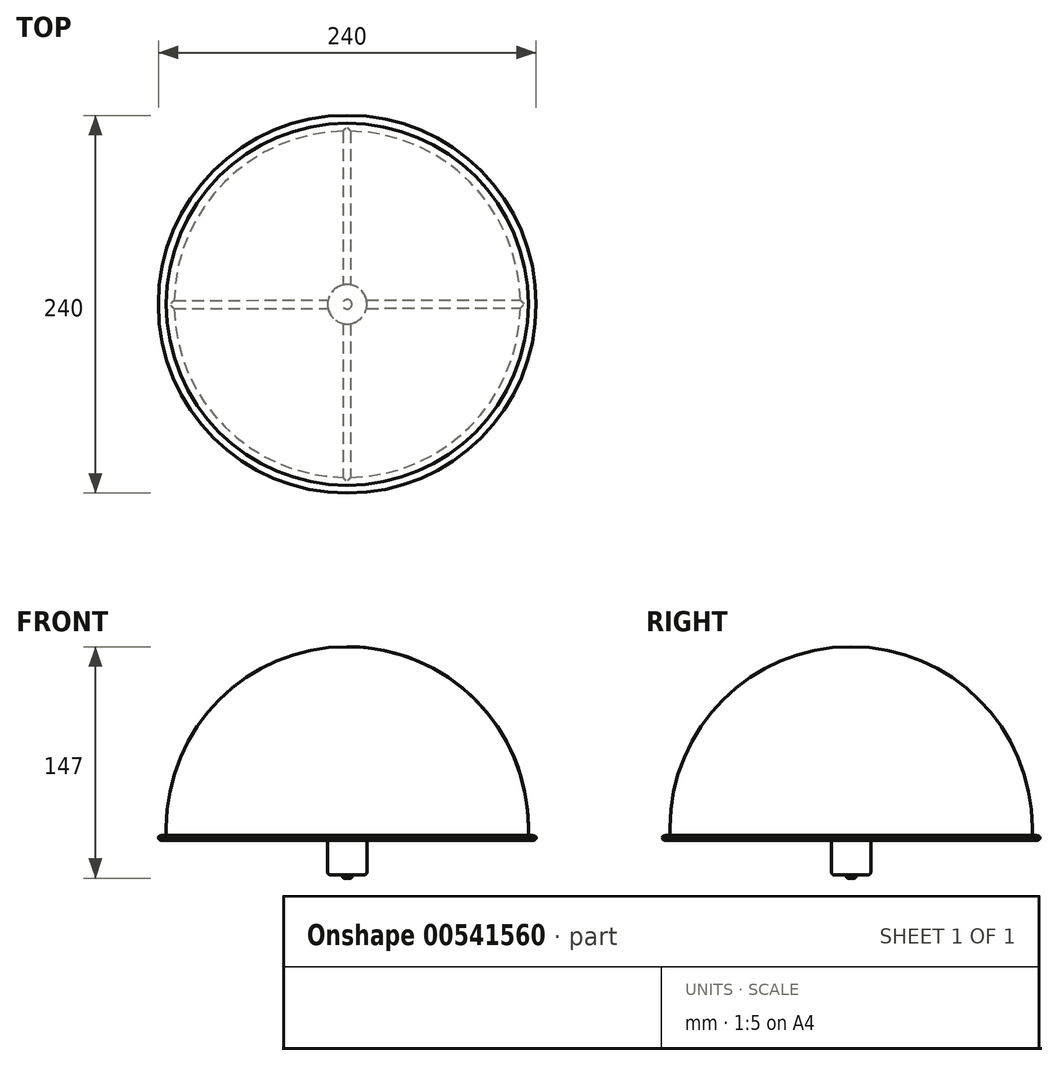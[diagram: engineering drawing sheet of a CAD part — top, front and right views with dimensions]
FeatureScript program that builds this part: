
annotation { "Feature Type Name" : "Feature", "Feature Type Description" : "" }
export const myFeature = defineFeature(function(context is Context, id is Id, definition is map)
    precondition{}
    {
        {
            var Q0;
            Q0=qCreatedBy(makeId("Top.planeOp"),FACE);
            var sketch = newSketch(context, id + "F0", { "sketchPlane" : qUnion([Q0])});
            skCircle(sketch, "E0", {"center": v(0, 0) * mm, "radius": 115 * mm});
            skSolve(sketch);
        }
        {
            var Q0;
            Q0 = qSketchRegion(id + "F0", true);
            extrude(context, id + "F1", {"entities" : qUnion([Q0]), "depth" : 120 * mm, "offsetDistance" : 25 * mm});
        }
        {
            var Q0;
            Q0=makeQuery(id+"F1.opExtrude","CAP_EDGE",EDGE,{"disambiguationData":[OSD([sQuery(id+"F0.wireOp",EDGE,"E0")])],"isStart":false});
            fillet(context, id + "F2", {"entities" : qUnion([Q0]), "radius" : 115 * mm, "tangentPropagation" : true, "allowEdgeOverflow" : false});
        }
        {
            var Q0;
            Q0=makeQuery(id+"F1.opExtrude","CAP_FACE",FACE,{"disambiguationData":[OSD([sQuery(id+"F0.wireOp",EDGE,"E0")])],"isStart":true});
            var sketch = newSketch(context, id + "F3", { "sketchPlane" : qUnion([Q0])});
            skCircle(sketch, "E1", {"center": v(0, 0) * mm, "radius": 120 * mm});
            skArc(sketch, "E2", {"start": v(2.2, -109.98) * mm, "mid": v(77.64, -77.93) * mm, "end": v(109.97, -2.6) * mm});
            skLineSegment(sketch, "E3.left", {"start": v(-2.8, -109.96) * mm, "end": v(-2.8, -2.56) * mm});
            skLineSegment(sketch, "E3.right", {"start": v(2.2, -109.98) * mm, "end": v(2.2, -2.56) * mm});
            skPoint(sketch, "E3.middle", {"position": v(-0.3, 15.02) * mm});
            skLineSegment(sketch, "E4.1.0", {"start": v(-109.97, -2.5) * mm, "end": v(-2.8, -2.56) * mm});
            skLineSegment(sketch, "E4.1.1", {"start": v(-109.96, 2.8) * mm, "end": v(-2.8, 2.6) * mm});
            skLineSegment(sketch, "E4.anchor1", {"start": v(0, 0) * mm, "end": v(2.4, -119.98) * mm, "construction": true});
            skLineSegment(sketch, "E4.anchor2", {"start": v(0, 0) * mm, "end": v(-125, -2.5) * mm, "construction": true});
            skPoint(sketch, "E5.orphan", {"position": v(2.2, -109.98) * mm});
            skPoint(sketch, "E6.orphan", {"position": v(-2.8, -109.97) * mm});
            skPoint(sketch, "E7.orphan", {"position": v(125, 2.36) * mm});
            skPoint(sketch, "E8.orphan", {"position": v(129.97, -2.62) * mm});
            skArc(sketch, "E9.trimOffspring", {"start": v(109.97, 2.4) * mm, "mid": v(77.71, 77.85) * mm, "end": v(2.2, 109.98) * mm});
            skPoint(sketch, "E10.orphan", {"position": v(2.2, 140.01) * mm});
            skPoint(sketch, "E11.orphan", {"position": v(-2.8, 140.02) * mm});
            skArc(sketch, "E12.trimOffspring", {"start": v(-2.8, 109.96) * mm, "mid": v(-77.78, 77.78) * mm, "end": v(-109.96, 2.8) * mm});
            skArc(sketch, "E13.trimOffspring", {"start": v(-109.98, -2.2) * mm, "mid": v(-78, -77.57) * mm, "end": v(-2.8, -109.96) * mm});
            skLineSegment(sketch, "E14.trimOffspring", {"start": v(2.2, 2.6) * mm, "end": v(2.2, 109.98) * mm});
            skLineSegment(sketch, "E15.trimOffspring", {"start": v(2.2, 2.6) * mm, "end": v(109.97, 2.4) * mm});
            skLineSegment(sketch, "E16.trimOffspring", {"start": v(-2.8, 2.6) * mm, "end": v(-2.8, 109.96) * mm});
            skLineSegment(sketch, "E17.trimOffspring", {"start": v(2.2, -2.56) * mm, "end": v(109.97, -2.6) * mm});
            skSolve(sketch);
        }
        {
            var Q0;
            Q0 = qSketchRegion(id + "F3", true);
            extrude(context, id + "F4", {"entities" : qUnion([Q0]), "operationType" : NewBodyOperationType.ADD, "depth" : 3 * mm, "offsetDistance" : 25 * mm});
        }
        {
            var Q0;
            Q0=makeQuery(id+"F4.opExtrude","CAP_EDGE",EDGE,{"disambiguationData":[OSD([sQuery(id+"F3.wireOp",EDGE,"E4.1.1")])],"isStart":false});
            var Q1;
            Q1=makeQuery(id+"F4.opExtrude","CAP_EDGE",EDGE,{"disambiguationData":[OSD([sQuery(id+"F3.wireOp",EDGE,"E4.1.0")])],"isStart":false});
            var Q2;
            Q2=makeQuery(id+"F4.opExtrude","CAP_EDGE",EDGE,{"disambiguationData":[OSD([sQuery(id+"F3.wireOp",EDGE,"E3.left")])],"isStart":false});
            var Q3;
            Q3=makeQuery(id+"F4.opExtrude","CAP_EDGE",EDGE,{"disambiguationData":[OSD([sQuery(id+"F3.wireOp",EDGE,"E3.right")])],"isStart":false});
            var Q4;
            Q4=makeQuery(id+"F4.opExtrude","CAP_EDGE",EDGE,{"disambiguationData":[OSD([sQuery(id+"F3.wireOp",EDGE,"E15.trimOffspring")])],"isStart":false});
            var Q5;
            Q5=makeQuery(id+"F4.opExtrude","CAP_EDGE",EDGE,{"disambiguationData":[OSD([sQuery(id+"F3.wireOp",EDGE,"E17.trimOffspring")])],"isStart":false});
            var Q6;
            Q6=makeQuery(id+"F4.opExtrude","CAP_EDGE",EDGE,{"disambiguationData":[OSD([sQuery(id+"F3.wireOp",EDGE,"E14.trimOffspring")])],"isStart":false});
            var Q7;
            Q7=makeQuery(id+"F4.opExtrude","CAP_EDGE",EDGE,{"disambiguationData":[OSD([sQuery(id+"F3.wireOp",EDGE,"E16.trimOffspring")])],"isStart":false});
            var Q8;
            Q8=makeQuery(id+"F4.opExtrude","CAP_EDGE",EDGE,{"disambiguationData":[OSD([sQuery(id+"F3.wireOp",EDGE,"E12.trimOffspring")])],"isStart":false});
            var Q9;
            Q9=makeQuery(id+"F4.opExtrude","CAP_EDGE",EDGE,{"disambiguationData":[OSD([sQuery(id+"F3.wireOp",EDGE,"E13.trimOffspring")])],"isStart":false});
            var Q10;
            Q10=makeQuery(id+"F4.opExtrude","CAP_EDGE",EDGE,{"disambiguationData":[OSD([sQuery(id+"F3.wireOp",EDGE,"E1")])],"isStart":false});
            var Q11;
            Q11=makeQuery(id+"F4.opExtrude","CAP_EDGE",EDGE,{"disambiguationData":[OSD([sQuery(id+"F3.wireOp",EDGE,"E9.trimOffspring")])],"isStart":false});
            var Q12;
            Q12=makeQuery(id+"F4.opExtrude","CAP_EDGE",EDGE,{"disambiguationData":[OSD([sQuery(id+"F3.wireOp",EDGE,"E2")])],"isStart":false});
            fillet(context, id + "F5", {"entities" : qUnion([Q0, Q1, Q2, Q3, Q4, Q5, Q6, Q7, Q8, Q9, Q10, Q11, Q12]), "radius" : 2 * mm, "tangentPropagation" : true, "allowEdgeOverflow" : false});
        }
        {
            var Q0;
            Q0=makeQuery(id+"F4.opExtrude","CAP_EDGE",EDGE,{"disambiguationData":[OSD([sQuery(id+"F3.wireOp",EDGE,"E1")])],"isStart":true});
            fillet(context, id + "F6", {"entities" : qUnion([Q0]), "radius" : 2.5 * mm, "tangentPropagation" : true, "allowEdgeOverflow" : false});
        }
        {
            var Q0;
            Q0=makeQuery(id+"F4.boolean.opBoolean","SPLIT",FACE,{"disambiguationData":[TD([makeQuery(id+"F4.opExtrude","SWEPT_FACE",FACE,{"disambiguationData":[OSD([sQuery(id+"F3.wireOp",EDGE,"E9.trimOffspring")])]})])],"derivedFrom":makeQuery(id+"F1.opExtrude","CAP_FACE",FACE,{"disambiguationData":[OSD([sQuery(id+"F0.wireOp",EDGE,"E0")])],"isStart":true})});
            var sketch = newSketch(context, id + "F7", { "sketchPlane" : qUnion([Q0])});
            skCircle(sketch, "E18", {"center": v(0, 0) * mm, "radius": 12.5 * mm});
            skSolve(sketch);
        }
        {
            var Q0;
            Q0 = qSketchRegion(id + "F7", true);
            extrude(context, id + "F8", {"entities" : qUnion([Q0]), "operationType" : NewBodyOperationType.ADD, "depth" : 25 * mm, "offsetDistance" : 25 * mm});
        }
        {
            var Q0;
            Q0=makeQuery(id+"F8.opExtrude","CAP_FACE",FACE,{"disambiguationData":[OSD([sQuery(id+"F7.wireOp",EDGE,"E18")])],"isStart":false});
            var sketch = newSketch(context, id + "F9", { "sketchPlane" : qUnion([Q0])});
            skCircle(sketch, "E19", {"center": v(0, 0) * mm, "radius": 3 * mm});
            skSolve(sketch);
        }
        {
            var Q0;
            Q0 = qSketchRegion(id + "F9", true);
            extrude(context, id + "F10", {"entities" : qUnion([Q0]), "operationType" : NewBodyOperationType.ADD, "depth" : 2 * mm, "offsetDistance" : 25 * mm});
        }
        {
            var Q0;
            Q0=makeQuery(id+"F10.opExtrude","CAP_EDGE",EDGE,{"disambiguationData":[OSD([sQuery(id+"F9.wireOp",EDGE,"E19")])],"isStart":false});
            fillet(context, id + "F11", {"entities" : qUnion([Q0]), "radius" : 1 * mm, "tangentPropagation" : true, "allowEdgeOverflow" : false});
        }
        {
            var Q0;
            Q0=makeQuery(id+"F8.opExtrude","CAP_EDGE",EDGE,{"disambiguationData":[OSD([sQuery(id+"F7.wireOp",EDGE,"E18")])],"isStart":false});
            fillet(context, id + "F12", {"entities" : qUnion([Q0]), "radius" : 2 * mm, "tangentPropagation" : true, "allowEdgeOverflow" : false});
        }
    });
